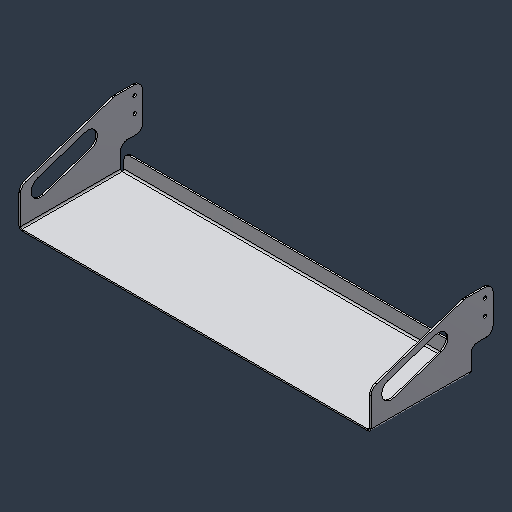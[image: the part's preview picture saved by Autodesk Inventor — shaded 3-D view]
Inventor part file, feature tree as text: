
AUTODESK INVENTOR PART (.ipt)
format: ipt  version: 2024.3 (Build 283343000, 343)  size: 125,952 bytes
history: native  units: mm (DEFAULTED — no unit token found)
features: fillet x1
ambient origin geometry x8: Origin, YZ Plane, XZ Plane, XY Plane, X Axis, Y Axis, Z Axis, Center Point
bodies: Solid1 (feature_tree)
feature tree (1):
  fillet  "Fillet2"  [1 undecoded]
note: 1 required parameter value undecoded (feature->parameter linkage not recoverable at this tier; creation-order binding heuristic only, values carry confidence <= 0.55)
